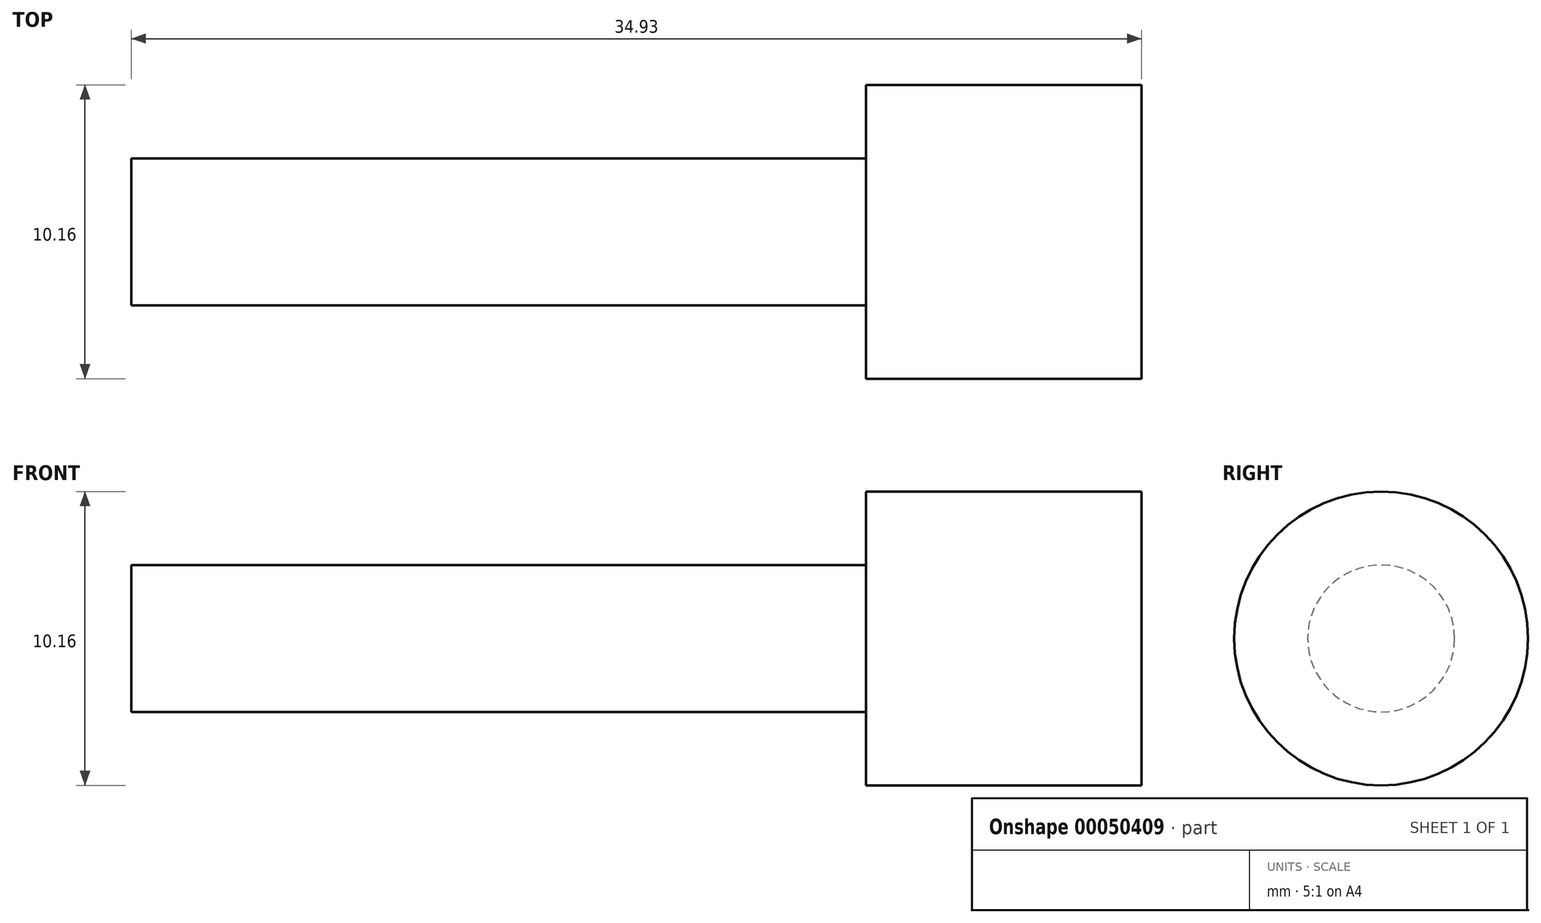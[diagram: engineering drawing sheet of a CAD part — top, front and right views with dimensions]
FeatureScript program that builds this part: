
annotation { "Feature Type Name" : "Feature", "Feature Type Description" : "" }
export const myFeature = defineFeature(function(context is Context, id is Id, definition is map)
    precondition{}
    {
        {
            var Q0;
            Q0=qCreatedBy(makeId("Front.planeOp"),FACE);
            var sketch = newSketch(context, id + "F0", { "sketchPlane" : qUnion([Q0])});
            skLineSegment(sketch, "E0.bottom", {"start": v(0, 0) * mm, "end": v(34.93, 0) * mm});
            skLineSegment(sketch, "E0.top", {"start": v(0, 2.54) * mm, "end": v(25.4, 2.54) * mm});
            skLineSegment(sketch, "E0.left", {"start": v(0, 0) * mm, "end": v(0, 2.54) * mm});
            skLineSegment(sketch, "E0.right", {"start": v(34.93, 0) * mm, "end": v(34.93, 2.54) * mm});
            skPoint(sketch, "E1", {"position": v(25.4, 2.54) * mm});
            skLineSegment(sketch, "E2.top", {"start": v(25.4, 5.08) * mm, "end": v(34.93, 5.08) * mm});
            skLineSegment(sketch, "E2.left", {"start": v(25.4, 2.54) * mm, "end": v(25.4, 5.08) * mm});
            skLineSegment(sketch, "E2.right", {"start": v(34.93, 2.54) * mm, "end": v(34.93, 5.08) * mm});
            skSolve(sketch);
        }
        {
            var Q0;
            Q0 = qSketchRegion(id + "F0", true);
            var Q1;
            Q1=makeQuery(id+"F0.imprint","IMPRINT",FACE,{"disambiguationData":[TD([[makeQuery(id+"F0.imprint","IMPRINT",EDGE,{"derivedFrom":sQuery(id+"F0.wireOp",EDGE,"E0.bottom")}),1.0]])]});
            var Q2;
            Q2=sQuery(id+"F0.wireOp",EDGE,"E0.bottom");
            revolve(context, id + "F1", {"entities" : qUnion([Q0, Q1]), "axis" : qUnion([Q2]), "revolveType" : RevolveType.FULL});
        }
    });
